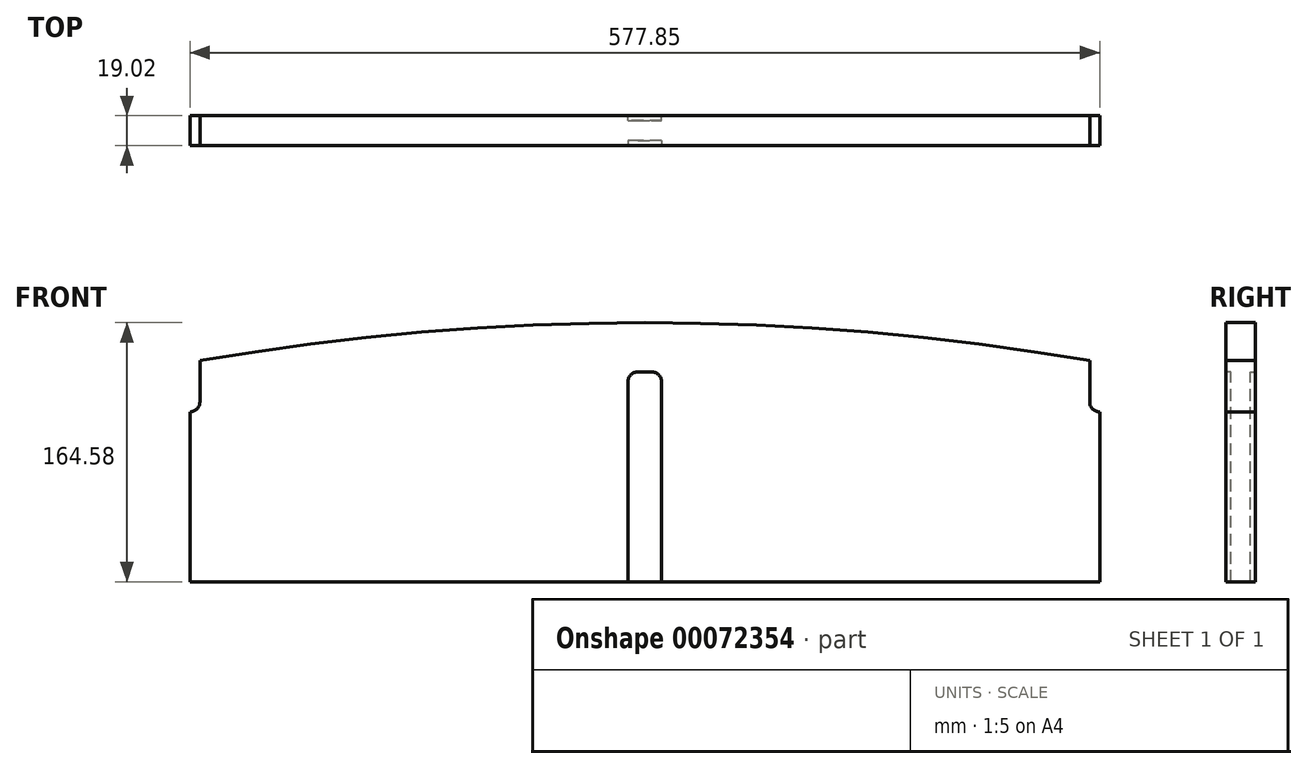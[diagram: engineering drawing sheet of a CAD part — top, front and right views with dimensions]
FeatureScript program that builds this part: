
annotation { "Feature Type Name" : "Feature", "Feature Type Description" : "" }
export const myFeature = defineFeature(function(context is Context, id is Id, definition is map)
    precondition{}
    {
        {
            var Q0;
            Q0=qCreatedBy(makeId("Front.planeOp"),FACE);
            var sketch = newSketch(context, id + "F0", { "sketchPlane" : qUnion([Q0])});
            skLineSegment(sketch, "E0.rect.bottom", {"start": v(285.75, -70.25) * mm, "end": v(-292.1, -70.25) * mm});
            skLineSegment(sketch, "E0.rect.left", {"start": v(285.75, -70.25) * mm, "end": v(285.75, 37.7) * mm});
            skLineSegment(sketch, "E0.rect.right", {"start": v(-292.1, -70.25) * mm, "end": v(-292.1, 37.7) * mm});
            skPoint(sketch, "E0.rect.middle", {"position": v(0, 0) * mm});
            skArc(sketch, "E1", {"start": v(279.4, 70.25) * mm, "mid": v(-3.18, 94.33) * mm, "end": v(-285.75, 70.25) * mm});
            skLineSegment(sketch, "E2.bottom", {"start": v(285.75, 37.7) * mm, "end": v(285.75, 37.7) * mm});
            skLineSegment(sketch, "E2.right", {"start": v(279.4, 44.05) * mm, "end": v(279.4, 70.25) * mm});
            skPoint(sketch, "E3.visualSharp", {"position": v(279.4, 37.7) * mm});
            skArc(sketch, "E3.filletArc", {"start": v(279.4, 44.05) * mm, "mid": v(281.26, 39.56) * mm, "end": v(285.75, 37.7) * mm});
            skLineSegment(sketch, "E4", {"start": v(-3.17, -70.25) * mm, "end": v(-3.17, 119.27) * mm, "construction": true});
            skPoint(sketch, "E4.endSnap0", {"position": v(-3.17, -70.25) * mm});
            skArc(sketch, "E5.MirrorCS", {"start": v(-285.75, 44.05) * mm, "mid": v(-287.61, 39.56) * mm, "end": v(-292.1, 37.7) * mm});
            skLineSegment(sketch, "E6.MirrorCS", {"start": v(-285.75, 44.05) * mm, "end": v(-285.75, 70.25) * mm});
            skSolve(sketch);
        }
        {
            var Q0;
            Q0=makeQuery(id+"F0.imprint","IMPRINT",FACE,{"disambiguationData":[TD([[makeQuery(id+"F0.imprint","IMPRINT",EDGE,{"derivedFrom":sQuery(id+"F0.wireOp",EDGE,"E0.rect.bottom")}),-1.0]])]});
            extrude(context, id + "F1", {"entities" : qUnion([Q0]), "depth" : 19.02 * mm, "symmetric" : true});
        }
        {
            var Q0;
            Q0=makeQuery(id+"F1.opExtrude","CAP_FACE",FACE,{"disambiguationData":[OSD([sQuery(id+"F0.wireOp",EDGE,"E0.rect.bottom"),sQuery(id+"F0.wireOp",EDGE,"E0.rect.left"),sQuery(id+"F0.wireOp",EDGE,"E0.rect.right"),sQuery(id+"F0.wireOp",EDGE,"E1"),sQuery(id+"F0.wireOp",EDGE,"E2.right"),sQuery(id+"F0.wireOp",EDGE,"E3.filletArc"),sQuery(id+"F0.wireOp",EDGE,"E5.MirrorCS"),sQuery(id+"F0.wireOp",EDGE,"E6.MirrorCS")])],"isStart":false});
            var sketch = newSketch(context, id + "F2", { "sketchPlane" : qUnion([Q0])});
            skLineSegment(sketch, "E7.bottom", {"start": v(-13.9, -70.25) * mm, "end": v(7.54, -70.25) * mm, "construction": true});
            skLineSegment(sketch, "E7.top", {"start": v(-7.54, 63.1) * mm, "end": v(1.2, 63.1) * mm});
            skLineSegment(sketch, "E7.left", {"start": v(-13.9, -70.25) * mm, "end": v(-13.9, 56.75) * mm});
            skLineSegment(sketch, "E7.right", {"start": v(7.54, -70.25) * mm, "end": v(7.54, 56.75) * mm});
            skPoint(sketch, "E8.visualSharp", {"position": v(-13.9, 63.1) * mm});
            skArc(sketch, "E8.filletArc", {"start": v(-7.54, 63.1) * mm, "mid": v(-12.03, 61.24) * mm, "end": v(-13.9, 56.75) * mm});
            skPoint(sketch, "E9.visualSharp", {"position": v(7.54, 63.1) * mm});
            skArc(sketch, "E9.filletArc", {"start": v(7.54, 56.75) * mm, "mid": v(5.68, 61.24) * mm, "end": v(1.2, 63.1) * mm});
            skSolve(sketch);
        }
        {
            var Q0;
            Q0 = qSketchRegion(id + "F2", true);
            var Q1;
            Q1=makeQuery(id+"F2.imprint","IMPRINT",FACE,{"disambiguationData":[TD([[makeQuery(id+"F2.imprint","IMPRINT",EDGE,{"derivedFrom":sQuery(id+"F2.wireOp",EDGE,"E7.top")}),-1.0]])]});
            extrude(context, id + "F3", {"entities" : qUnion([Q0, Q1]), "operationType" : NewBodyOperationType.REMOVE, "oppositeDirection" : true, "depth" : 3.17 * mm});
        }
        {
            var Q0;
            Q0=makeQuery(id+"F1.opExtrude","CAP_FACE",FACE,{"disambiguationData":[OSD([sQuery(id+"F0.wireOp",EDGE,"E0.rect.bottom"),sQuery(id+"F0.wireOp",EDGE,"E0.rect.left"),sQuery(id+"F0.wireOp",EDGE,"E0.rect.right"),sQuery(id+"F0.wireOp",EDGE,"E1"),sQuery(id+"F0.wireOp",EDGE,"E2.right"),sQuery(id+"F0.wireOp",EDGE,"E3.filletArc"),sQuery(id+"F0.wireOp",EDGE,"E5.MirrorCS"),sQuery(id+"F0.wireOp",EDGE,"E6.MirrorCS")])],"isStart":true});
            var sketch = newSketch(context, id + "F4", { "sketchPlane" : qUnion([Q0])});
            skLineSegment(sketch, "E10.0", {"start": v(-7.54, -70.25) * mm, "end": v(-7.54, 56.75) * mm});
            skArc(sketch, "E11.0", {"start": v(-7.54, 56.75) * mm, "mid": v(-5.68, 61.24) * mm, "end": v(-1.2, 63.1) * mm});
            skLineSegment(sketch, "E12.0", {"start": v(7.54, 63.1) * mm, "end": v(-1.2, 63.1) * mm});
            skArc(sketch, "E13.0", {"start": v(7.54, 63.1) * mm, "mid": v(12.03, 61.24) * mm, "end": v(13.9, 56.75) * mm});
            skLineSegment(sketch, "E14.0", {"start": v(13.9, -70.25) * mm, "end": v(13.9, 56.75) * mm});
            skLineSegment(sketch, "E15.0", {"start": v(-7.54, -70.25) * mm, "end": v(13.9, -70.25) * mm});
            skSolve(sketch);
        }
        {
            var Q0;
            Q0=makeQuery(id+"F4.imprint","IMPRINT",FACE,{"disambiguationData":[TD([[makeQuery(id+"F4.imprint","IMPRINT",EDGE,{"derivedFrom":sQuery(id+"F4.wireOp",EDGE,"E10.0")}),-1.0]])]});
            extrude(context, id + "F5", {"entities" : qUnion([Q0]), "operationType" : NewBodyOperationType.REMOVE, "oppositeDirection" : true, "depth" : 3.17 * mm});
        }
    });
